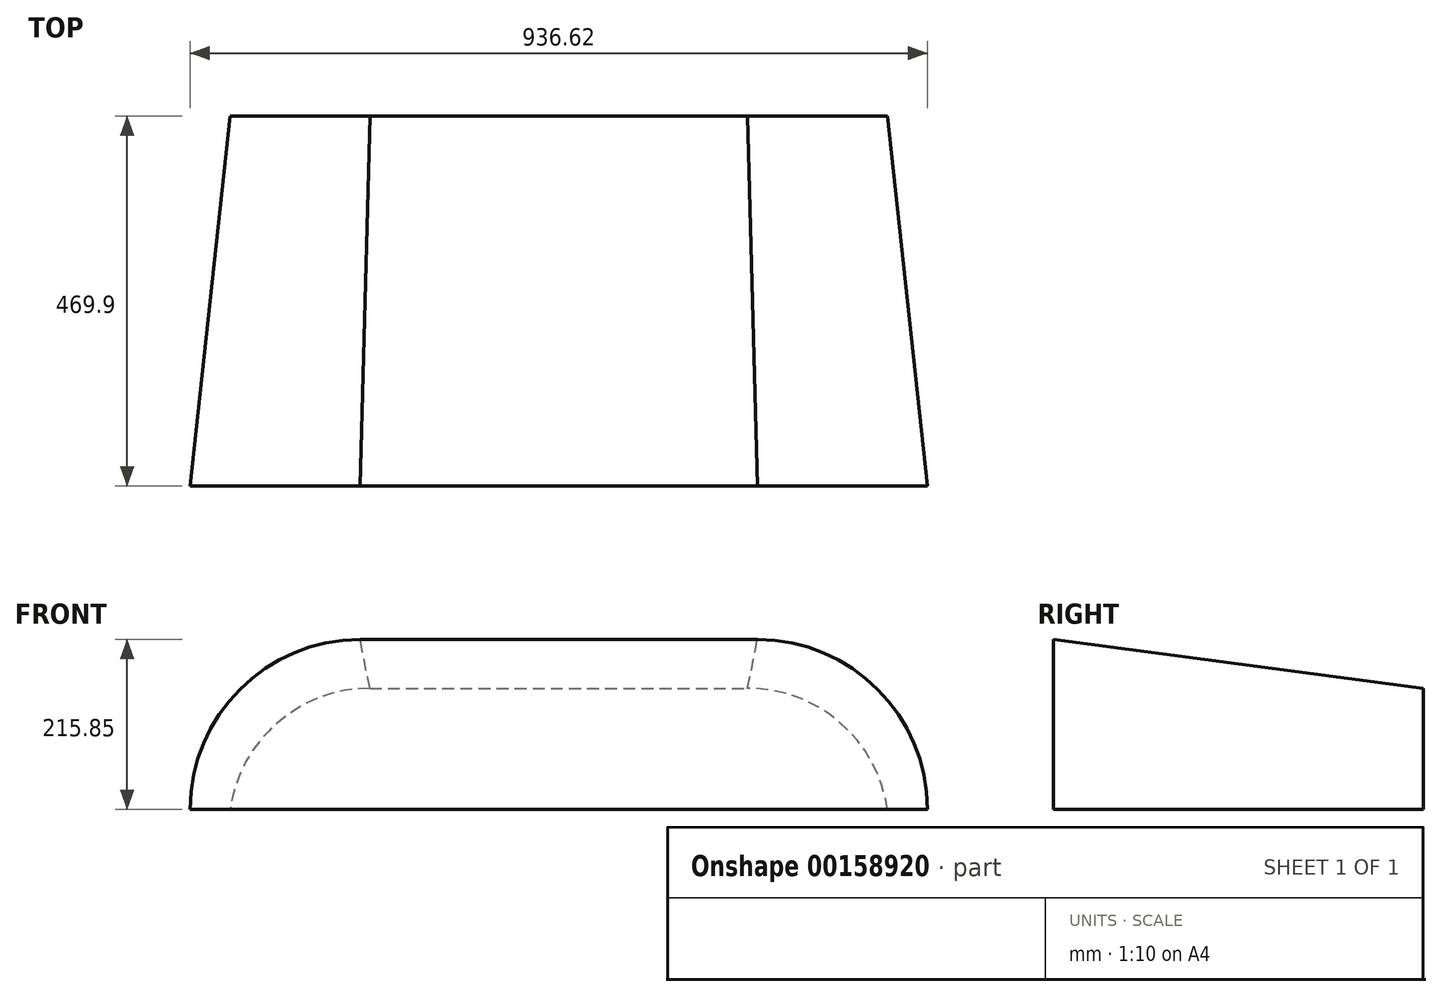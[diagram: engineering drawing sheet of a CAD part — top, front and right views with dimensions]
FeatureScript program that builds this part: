
annotation { "Feature Type Name" : "Feature", "Feature Type Description" : "" }
export const myFeature = defineFeature(function(context is Context, id is Id, definition is map)
    precondition{}
    {
        {
            var Q0;
            Q0=qCreatedBy(makeId("Top.planeOp"),FACE);
            var sketch = newSketch(context, id + "F0", { "sketchPlane" : qUnion([Q0])});
            skLineSegment(sketch, "E0", {"start": v(-417.51, 0) * mm, "end": v(417.51, 0) * mm});
            skLineSegment(sketch, "E1", {"start": v(-468.31, -469.9) * mm, "end": v(468.31, -469.9) * mm});
            skLineSegment(sketch, "E2", {"start": v(0, 0) * mm, "end": v(0, -469.9) * mm, "construction": true});
            skLineSegment(sketch, "E3", {"start": v(-417.51, 0) * mm, "end": v(-414.38, 23.81) * mm, "construction": true});
            skLineSegment(sketch, "E4", {"start": v(-414.38, 23.81) * mm, "end": v(414.38, 23.81) * mm, "construction": true});
            skLineSegment(sketch, "E5", {"start": v(414.38, 23.81) * mm, "end": v(417.51, 0) * mm, "construction": true});
            skFitSpline(sketch, "E6", {"points": [v(-417.51, 0) * mm, v(-468.31, -469.9) * mm], "startDerivative": vector(-72.99, -554.39) * mm, "endDerivative": vector(-50.8, -469.9) * mm});
            skFitSpline(sketch, "E7", {"points": [v(417.51, 0) * mm, v(468.31, -469.9) * mm], "startDerivative": vector(72.99, -554.39) * mm, "endDerivative": vector(50.8, -469.9) * mm});
            skSolve(sketch);
        }
        {
            var Q0;
            Q0=qCreatedBy(makeId("Front.planeOp"),FACE);
            var sketch = newSketch(context, id + "F1", { "sketchPlane" : qUnion([Q0])});
            skLineSegment(sketch, "E8", {"start": v(-239.93, 153.99) * mm, "end": v(239.93, 153.99) * mm});
            skLineSegment(sketch, "E9", {"start": v(-417.51, 0) * mm, "end": v(417.51, 0) * mm});
            skArc(sketch, "E10", {"start": v(417.51, 0) * mm, "mid": v(357.46, 110.13) * mm, "end": v(239.93, 153.99) * mm});
            skArc(sketch, "E11", {"start": v(-239.93, 153.99) * mm, "mid": v(-357.46, 110.13) * mm, "end": v(-417.51, 0) * mm});
            skSolve(sketch);
        }
        {
            var Q0;
            Q0=sQuery(id+"F1.wireOp",EDGE,"E8");
            var Q1;
            Q1=qCreatedBy(makeId("Front.planeOp"),FACE);
            cPlane(context, id + "F2", {"entities" : qUnion([Q0, Q1]), "cplaneType" : CPlaneType.LINE_ANGLE, "offset" : 25.4 * mm, "angle" : 82.5 * degree, "width" : 152.4 * mm, "height" : 152.4 * mm});
        }
        {
            var Q0;
            Q0=sQuery(id+"F0.wireOp",EDGE,"E1");
            var Q1;
            Q1=qCreatedBy(makeId("Front.planeOp"),FACE);
            cPlane(context, id + "F3", {"entities" : qUnion([Q0, Q1]), "cplaneType" : CPlaneType.LINE_ANGLE, "offset" : 25.4 * mm, "angle" : 0 * degree, "width" : 152.4 * mm, "height" : 152.4 * mm});
        }
        {
            var Q0;
            Q0=qCreatedBy(id+"F3.planeOp",FACE);
            var sketch = newSketch(context, id + "F4", { "sketchPlane" : qUnion([Q0])});
            skLineSegment(sketch, "E12", {"start": v(252.46, 215.85) * mm, "end": v(-252.46, 215.85) * mm});
            skLineSegment(sketch, "E13.0", {"start": v(468.31, 0) * mm, "end": v(-468.31, 0) * mm});
            skArc(sketch, "E14", {"start": v(468.31, 0) * mm, "mid": v(405.1, 152.63) * mm, "end": v(252.46, 215.85) * mm});
            skArc(sketch, "E15", {"start": v(-252.46, 215.85) * mm, "mid": v(-405.1, 152.63) * mm, "end": v(-468.31, 0) * mm});
            skLineSegment(sketch, "E16", {"start": v(-468.31, 0) * mm, "end": v(-468.31, -84.12) * mm, "construction": true});
            skLineSegment(sketch, "E17", {"start": v(468.31, 0) * mm, "end": v(468.31, -79.84) * mm, "construction": true});
            skSolve(sketch);
        }
        {
            var Q0;
            Q0 = qSketchRegion(id + "F1", true);
            var Q1;
            Q1 = qSketchRegion(id + "F4", true);
            loft(context, id + "F5", {"sheetProfilesArray" : [{ "sheetProfileEntities" : qUnion([Q0]) }, { "sheetProfileEntities" : qUnion([Q1]) }]});
        }
    });
